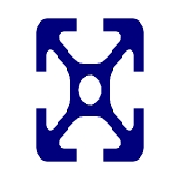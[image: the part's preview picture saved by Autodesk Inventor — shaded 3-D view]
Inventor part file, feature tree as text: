
AUTODESK INVENTOR PART (.ipt)
format: ipt  version: 2020 (Build 240168000, 168)  size: 277,504 bytes
history: native  units: mm
features: other x16, sketch x8, plane x1, split x1
ambient origin geometry x8: Origin, YZ Plane, XZ Plane, XY Plane, X Axis, Y Axis, Z Axis, Center Point
bodies: Body (feature_tree)
feature tree (26):
  other  "Řízená délka"
  other  "Těleso1"
  other  "Start Plane"
  other  "End Plane"
  other  "iFeatureSketch"
  other  "DRAZKA_20:1"
  other  "DRAZKA_20:2"
  other  "DRAZKA_20:3"
  other  "DRAZKA_20:4"
  other  "DIRA_20:1"
  other  "DRAZKA_20:1Axis"
  other  "DRAZKA_20:2Axis"
  other  "DRAZKA_20:3Axis"
  other  "DRAZKA_20:4Axis"
  other  "DIRA_20:1Axis"
  plane  "Work Plane5"
  split  "Split1"
  sketch  "Sketch"  dims[d2=20.0mm d3=20.0mm d4=2.0mm d9=10.0mm d10=100.0mm d11=0.13mm d12=0.0mm d15=0.83mm d16=0.83mm d17=9.8mm d18=3.0mm d19=4.55mm d20=45.0deg d21=5.2mm d22=1.8mm d24=1.0mm d26=0.83mm d27=0.83mm d28=9.8mm d29=3.0mm d30=4.55mm d31=45.0deg d32=5.2mm d33=1.8mm d35=1.0mm d37=0.83mm d38=0.83mm d39=9.8mm d40=3.0mm d41=4.55mm d42=45.0deg d43=5.2mm d44=1.8mm d46=1.0mm d48=0.83mm d49=0.83mm d50=9.8mm d51=3.0mm d52=4.55mm d53=45.0deg d54=5.2mm d55=1.8mm d57=1.0mm d59=4.3mm d60=0.0mm d61=0.0mm d62=0.0mm d63=0.0mm d64=0.0mm d65=0.0mm d66=0.0mm d67=0.0mm d76=90.0deg d14=90.0mm]
  sketch  "Náčrt11"
  other  "Pracovní rovina4"
  sketch  "Náčrt12"
  sketch  "Náčrt6"
  sketch  "Náčrt7"
  sketch  "Náčrt8"
  sketch  "Náčrt9"
  sketch  "Náčrt10"
